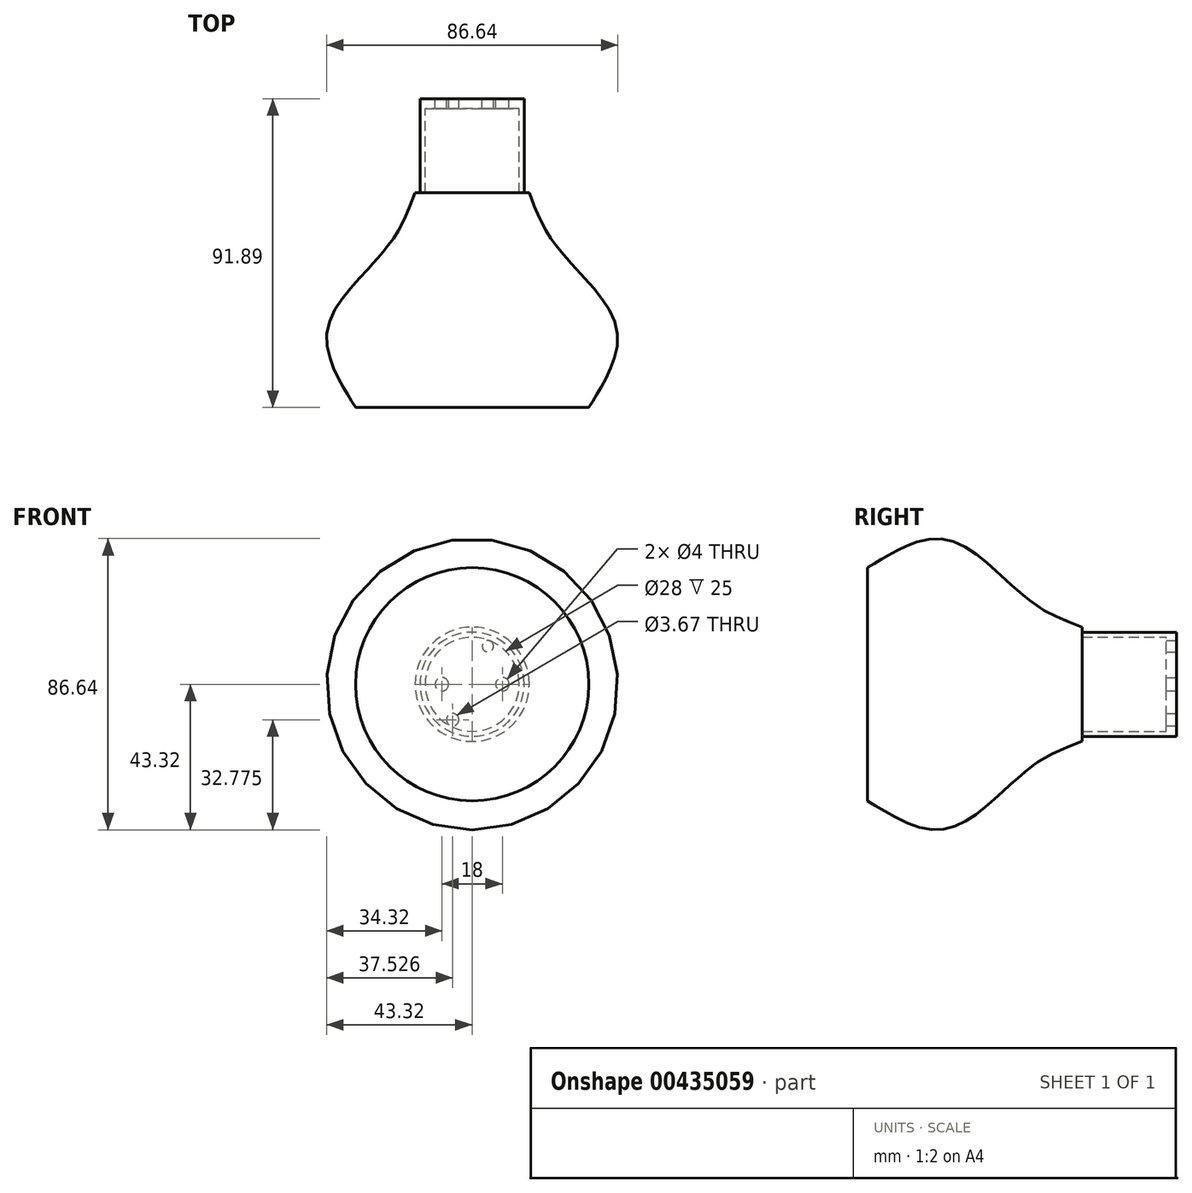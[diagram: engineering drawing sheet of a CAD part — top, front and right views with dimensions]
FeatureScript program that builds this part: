
annotation { "Feature Type Name" : "Feature", "Feature Type Description" : "" }
export const myFeature = defineFeature(function(context is Context, id is Id, definition is map)
    precondition{}
    {
        {
            var Q0;
            Q0=qCreatedBy(makeId("Front.planeOp"),FACE);
            var sketch = newSketch(context, id + "F0", { "sketchPlane" : qUnion([Q0])});
            skCircle(sketch, "E0", {"center": v(0, 0) * mm, "radius": 14 * mm});
            skLineSegment(sketch, "E1", {"start": v(-14, 0) * mm, "end": v(14, 0) * mm, "construction": true});
            skCircle(sketch, "E2", {"center": v(0, 0) * mm, "radius": 15.5 * mm});
            skCircle(sketch, "E3", {"center": v(9, 0) * mm, "radius": 2 * mm});
            skCircle(sketch, "E4", {"center": v(-9, 0) * mm, "radius": 2 * mm});
            skCircle(sketch, "E5", {"center": v(4.68, 11.31) * mm, "radius": 1.68 * mm});
            skCircle(sketch, "E6", {"center": v(-5.8, -10.54) * mm, "radius": 1.84 * mm});
            skSolve(sketch);
        }
        {
            var Q0;
            Q0 = qSketchRegion(id + "F0", true);
            extrude(context, id + "F1", {"entities" : qUnion([Q0]), "depth" : 28 * mm});
        }
        {
            var Q0;
            Q0=makeQuery(id+"F0.imprint","IMPRINT",FACE,{"disambiguationData":[TD([[makeQuery(id+"F0.imprint","IMPRINT",EDGE,{"derivedFrom":sQuery(id+"F0.wireOp",EDGE,"E0")}),1.0]])]});
            extrude(context, id + "F2", {"entities" : qUnion([Q0]), "operationType" : NewBodyOperationType.ADD, "depth" : 3 * mm});
        }
        {
            var Q0;
            Q0=qCreatedBy(makeId("Top.planeOp"),FACE);
            var sketch = newSketch(context, id + "F3", { "sketchPlane" : qUnion([Q0])});
            skLineSegment(sketch, "E7", {"start": v(0, -28) * mm, "end": v(-17, -28) * mm});
            skFitSpline(sketch, "E8", {"points": [v(-17, -28) * mm, v(-23.37, -41.48) * mm, v(-32.67, -52.53) * mm, v(-43.32, -71.4) * mm, v(-34.7, -91.89) * mm], "startDerivative": vector(-34.48, -91.7) * mm, "endDerivative": vector(27, -46.5) * mm});
            skLineSegment(sketch, "E9", {"start": v(-34.7, -91.89) * mm, "end": v(0, -91.89) * mm});
            skLineSegment(sketch, "E10", {"start": v(0, -91.89) * mm, "end": v(0, -28) * mm});
            skSolve(sketch);
        }
        {
            var Q0;
            Q0=makeQuery(id+"F3.imprint","IMPRINT",FACE,{"disambiguationData":[TD([[makeQuery(id+"F3.imprint","IMPRINT",EDGE,{"derivedFrom":sQuery(id+"F3.wireOp",EDGE,"E7")}),1.0]])]});
            var Q1;
            Q1=sQuery(id+"F3.wireOp",EDGE,"E10");
            revolve(context, id + "F4", {"entities" : qUnion([Q0]), "axis" : qUnion([Q1]), "revolveType" : RevolveType.FULL});
        }
    });
